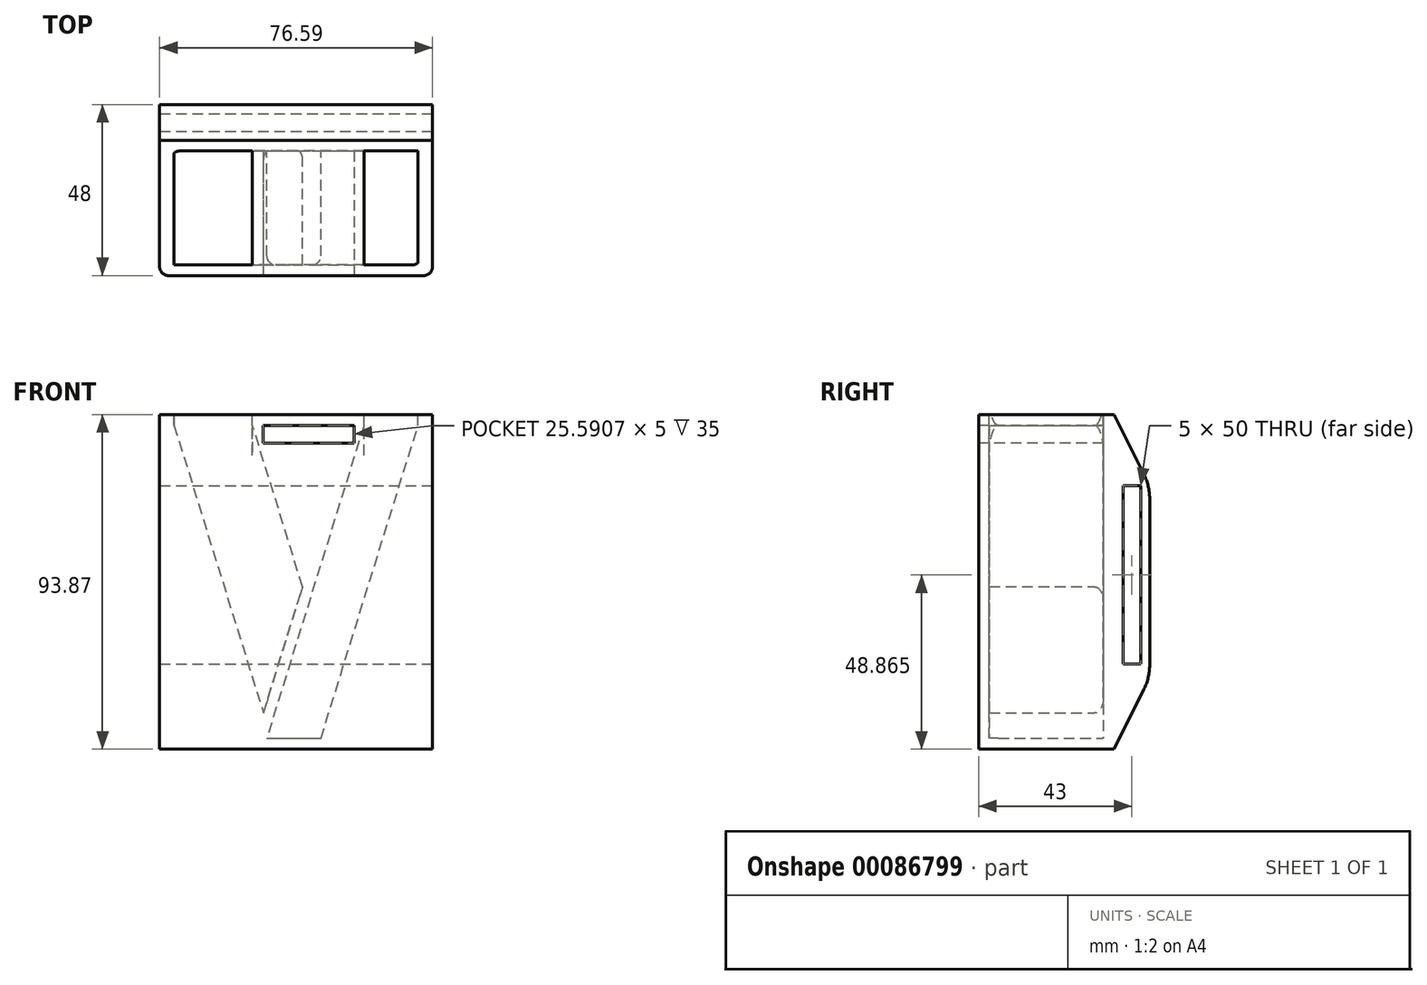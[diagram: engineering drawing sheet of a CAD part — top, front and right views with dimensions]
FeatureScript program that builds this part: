
annotation { "Feature Type Name" : "Feature", "Feature Type Description" : "" }
export const myFeature = defineFeature(function(context is Context, id is Id, definition is map)
    precondition{}
    {
        {
            var Q0;
            Q0=qCreatedBy(makeId("Front.planeOp"),FACE);
            var sketch = newSketch(context, id + "F0", { "sketchPlane" : qUnion([Q0])});
            skLineSegment(sketch, "E0", {"start": v(0, 0) * mm, "end": v(18.32, 0) * mm});
            skLineSegment(sketch, "E1", {"start": v(18.32, 0) * mm, "end": v(47.46, 93.87) * mm});
            skLineSegment(sketch, "E2", {"start": v(47.46, 93.87) * mm, "end": v(-29.13, 93.87) * mm});
            skLineSegment(sketch, "E3", {"start": v(-29.13, 93.87) * mm, "end": v(0, 0) * mm});
            skLineSegment(sketch, "E4", {"start": v(16.11, 3) * mm, "end": v(43.38, 90.87) * mm});
            skLineSegment(sketch, "E5", {"start": v(28.2, 90.87) * mm, "end": v(0.93, 3) * mm});
            skLineSegment(sketch, "E6", {"start": v(0, 10.12) * mm, "end": v(11, 45.54) * mm});
            skLineSegment(sketch, "E7", {"start": v(11, 45.54) * mm, "end": v(-3.07, 90.87) * mm});
            skLineSegment(sketch, "E8", {"start": v(-3.07, 90.87) * mm, "end": v(-25.06, 90.87) * mm, "construction": true});
            skLineSegment(sketch, "E9", {"start": v(-25.06, 90.87) * mm, "end": v(0, 10.12) * mm});
            skLineSegment(sketch, "E10", {"start": v(0.93, 3) * mm, "end": v(16.11, 3) * mm});
            skLineSegment(sketch, "E11", {"start": v(28.2, 90.87) * mm, "end": v(43.38, 90.87) * mm, "construction": true});
            skLineSegment(sketch, "E12", {"start": v(-14.07, 90.87) * mm, "end": v(5.5, 27.83) * mm, "construction": true});
            skLineSegment(sketch, "E13", {"start": v(-3.07, 90.87) * mm, "end": v(-3.07, 93.87) * mm});
            skLineSegment(sketch, "E14", {"start": v(-25.06, 90.87) * mm, "end": v(-25.06, 93.87) * mm});
            skLineSegment(sketch, "E15", {"start": v(28.2, 90.87) * mm, "end": v(28.2, 93.87) * mm});
            skLineSegment(sketch, "E16", {"start": v(43.38, 90.87) * mm, "end": v(43.38, 93.87) * mm});
            skLineSegment(sketch, "E17", {"start": v(-29.13, 93.87) * mm, "end": v(-29.13, 0) * mm});
            skLineSegment(sketch, "E18", {"start": v(-29.13, 0) * mm, "end": v(0, 0) * mm});
            skLineSegment(sketch, "E19", {"start": v(18.32, 0) * mm, "end": v(47.46, 0) * mm});
            skLineSegment(sketch, "E20", {"start": v(47.46, 0) * mm, "end": v(47.46, 93.87) * mm});
            skSolve(sketch);
        }
        {
            var Q0;
            Q0=makeQuery(id+"F0.imprint","IMPRINT",FACE,{"disambiguationData":[TD([[makeQuery(id+"F0.imprint","IMPRINT",EDGE,{"derivedFrom":sQuery(id+"F0.wireOp",EDGE,"E0")}),1.0]])]});
            var Q1;
            Q1=makeQuery(id+"F0.imprint","IMPRINT",FACE,{"disambiguationData":[TD([[makeQuery(id+"F0.imprint","IMPRINT",EDGE,{"derivedFrom":sQuery(id+"F0.wireOp",EDGE,"E6")}),1.0]])]});
            var Q2;
            Q2=makeQuery(id+"F0.imprint","IMPRINT",FACE,{"disambiguationData":[TD([[makeQuery(id+"F0.imprint","IMPRINT",EDGE,{"derivedFrom":sQuery(id+"F0.wireOp",EDGE,"E4")}),1.0]])]});
            var Q3;
            Q3=makeQuery(id+"F0.imprint","IMPRINT",FACE,{"disambiguationData":[TD([[makeQuery(id+"F0.imprint","IMPRINT",EDGE,{"derivedFrom":sQuery(id+"F0.wireOp",EDGE,"E3")}),-1.0]])]});
            var Q4;
            Q4=makeQuery(id+"F0.imprint","IMPRINT",FACE,{"disambiguationData":[TD([[makeQuery(id+"F0.imprint","IMPRINT",EDGE,{"derivedFrom":sQuery(id+"F0.wireOp",EDGE,"E1")}),-1.0]])]});
            extrude(context, id + "F1", {"entities" : qUnion([Q0, Q1, Q2, Q3, Q4]), "depth" : 3 * mm});
        }
        {
            var Q0;
            Q0=makeQuery(id+"F0.imprint","IMPRINT",FACE,{"disambiguationData":[TD([[makeQuery(id+"F0.imprint","IMPRINT",EDGE,{"derivedFrom":sQuery(id+"F0.wireOp",EDGE,"E0")}),1.0]])]});
            var Q1;
            Q1=makeQuery(id+"F0.imprint","IMPRINT",FACE,{"disambiguationData":[TD([[makeQuery(id+"F0.imprint","IMPRINT",EDGE,{"derivedFrom":sQuery(id+"F0.wireOp",EDGE,"E3")}),-1.0]])]});
            var Q2;
            Q2=makeQuery(id+"F0.imprint","IMPRINT",FACE,{"disambiguationData":[TD([[makeQuery(id+"F0.imprint","IMPRINT",EDGE,{"derivedFrom":sQuery(id+"F0.wireOp",EDGE,"E1")}),-1.0]])]});
            extrude(context, id + "F2", {"entities" : qUnion([Q0, Q1, Q2]), "operationType" : NewBodyOperationType.ADD, "depth" : 35 * mm, "hasSecondDirection" : true, "secondDirectionOppositeDirection" : false, "secondDirectionDepth" : 3 * mm});
        }
        {
            var Q0;
            Q0=makeQuery(id+"F0.imprint","IMPRINT",FACE,{"disambiguationData":[TD([[makeQuery(id+"F0.imprint","IMPRINT",EDGE,{"derivedFrom":sQuery(id+"F0.wireOp",EDGE,"E0")}),1.0]])]});
            var Q1;
            Q1=makeQuery(id+"F0.imprint","IMPRINT",FACE,{"disambiguationData":[TD([[makeQuery(id+"F0.imprint","IMPRINT",EDGE,{"derivedFrom":sQuery(id+"F0.wireOp",EDGE,"E6")}),1.0]])]});
            var Q2;
            Q2=makeQuery(id+"F0.imprint","IMPRINT",FACE,{"disambiguationData":[TD([[makeQuery(id+"F0.imprint","IMPRINT",EDGE,{"derivedFrom":sQuery(id+"F0.wireOp",EDGE,"E4")}),1.0]])]});
            var Q3;
            Q3=makeQuery(id+"F0.imprint","IMPRINT",FACE,{"disambiguationData":[TD([[makeQuery(id+"F0.imprint","IMPRINT",EDGE,{"derivedFrom":sQuery(id+"F0.wireOp",EDGE,"E3")}),-1.0]])]});
            var Q4;
            Q4=makeQuery(id+"F0.imprint","IMPRINT",FACE,{"disambiguationData":[TD([[makeQuery(id+"F0.imprint","IMPRINT",EDGE,{"derivedFrom":sQuery(id+"F0.wireOp",EDGE,"E1")}),-1.0]])]});
            extrude(context, id + "F3", {"entities" : qUnion([Q0, Q1, Q2, Q3, Q4]), "operationType" : NewBodyOperationType.ADD, "depth" : 38 * mm, "hasSecondDirection" : true, "secondDirectionOppositeDirection" : false, "secondDirectionDepth" : 35 * mm});
        }
        {
            var Q0;
            {var subQ0=sQuery(id+"F0.wireOp",EDGE,"E20");Q0=makeQuery(id+"F3.boolean.opBoolean","MERGE",FACE,{"derivedFrom":[makeQuery(id+"F2.boolean.opBoolean","MERGE",FACE,{"derivedFrom":[makeQuery(id+"F1.opExtrude","SWEPT_FACE",FACE,{"disambiguationData":[OSD([subQ0])]}),makeQuery(id+"F2.opExtrude","SWEPT_FACE",FACE,{"disambiguationData":[OSD([subQ0])]})]}),makeQuery(id+"F3.opExtrude","SWEPT_FACE",FACE,{"disambiguationData":[OSD([subQ0])]})]});}
            var sketch = newSketch(context, id + "F4", { "sketchPlane" : qUnion([Q0])});
            skLineSegment(sketch, "E21", {"start": v(0, 93.87) * mm, "end": v(10, 73.87) * mm});
            skLineSegment(sketch, "E22", {"start": v(10, 73.87) * mm, "end": v(10, 20) * mm});
            skLineSegment(sketch, "E23", {"start": v(10, 20) * mm, "end": v(0, 0) * mm});
            skLineSegment(sketch, "E24.bottom", {"start": v(2.5, 73.87) * mm, "end": v(7.5, 73.87) * mm});
            skLineSegment(sketch, "E24.top", {"start": v(2.5, 23.87) * mm, "end": v(7.5, 23.87) * mm});
            skLineSegment(sketch, "E24.left", {"start": v(2.5, 73.87) * mm, "end": v(2.5, 23.87) * mm});
            skLineSegment(sketch, "E24.right", {"start": v(7.5, 73.87) * mm, "end": v(7.5, 23.87) * mm});
            skSolve(sketch);
        }
        {
            var Q0;
            Q0=makeQuery(id+"F4.imprint","IMPRINT",FACE,{"disambiguationData":[TD([[makeQuery(id+"F4.imprint","IMPRINT",EDGE,{"derivedFrom":sQuery(id+"F4.wireOp",EDGE,"E21")}),-1.0]])]});
            var Q1;
            {var subQ0=sQuery(id+"F0.wireOp",EDGE,"E17");Q1=makeQuery(id+"F3.boolean.opBoolean","MERGE",FACE,{"derivedFrom":[makeQuery(id+"F2.boolean.opBoolean","MERGE",FACE,{"derivedFrom":[makeQuery(id+"F1.opExtrude","SWEPT_FACE",FACE,{"disambiguationData":[OSD([subQ0])]}),makeQuery(id+"F2.opExtrude","SWEPT_FACE",FACE,{"disambiguationData":[OSD([subQ0])]})]}),makeQuery(id+"F3.opExtrude","SWEPT_FACE",FACE,{"disambiguationData":[OSD([subQ0])]})]});}
            extrude(context, id + "F5", {"entities" : qUnion([Q0]), "operationType" : NewBodyOperationType.ADD, "endBound" : BoundingType.UP_TO_SURFACE, "oppositeDirection" : true, "endBoundEntityFace" : qUnion([Q1]), "depth" : 25 * mm});
        }
        {
            var Q0;
            Q0=makeQuery(id+"F5.opExtrude","SWEPT_EDGE",EDGE,{"disambiguationData":[OSD([sQuery(id+"F4.wireOp",EDGE,"E21"),sQuery(id+"F4.wireOp",EDGE,"E22")])]});
            var Q1;
            Q1=makeQuery(id+"F5.opExtrude","SWEPT_EDGE",EDGE,{"disambiguationData":[OSD([sQuery(id+"F4.wireOp",EDGE,"E22"),sQuery(id+"F4.wireOp",EDGE,"E23")])]});
            fillet(context, id + "F6", {"entities" : qUnion([Q0, Q1]), "radius" : 15 * mm, "tangentPropagation" : true, "allowEdgeOverflow" : false});
        }
        {
            var Q0;
            Q0=makeQuery(id+"F3.opExtrude","CAP_FACE",FACE,{"disambiguationData":[OSD([sQuery(id+"F0.wireOp",EDGE,"E0"),sQuery(id+"F0.wireOp",EDGE,"E2"),sQuery(id+"F0.wireOp",EDGE,"E17"),sQuery(id+"F0.wireOp",EDGE,"E18"),sQuery(id+"F0.wireOp",EDGE,"E19"),sQuery(id+"F0.wireOp",EDGE,"E20")])],"isStart":false});
            var sketch = newSketch(context, id + "F7", { "sketchPlane" : qUnion([Q0])});
            skLineSegment(sketch, "E25.right", {"start": v(25.46, 90.87) * mm, "end": v(25.46, 85.87) * mm});
            skLineSegment(sketch, "E26", {"start": v(25.46, 85.87) * mm, "end": v(-0.13, 85.87) * mm});
            skLineSegment(sketch, "E27", {"start": v(-0.13, 85.87) * mm, "end": v(-0.13, 90.87) * mm});
            skLineSegment(sketch, "E28", {"start": v(-0.13, 90.87) * mm, "end": v(25.46, 90.87) * mm});
            skSolve(sketch);
        }
        {
            var Q0;
            Q0=makeQuery(id+"F2.opExtrude","CAP_EDGE",EDGE,{"disambiguationData":[OSD([sQuery(id+"F0.wireOp",EDGE,"E9")])],"isStart":true});
            var Q1;
            Q1=makeQuery(id+"F2.opExtrude","CAP_EDGE",EDGE,{"disambiguationData":[OSD([sQuery(id+"F0.wireOp",EDGE,"E7")])],"isStart":true});
            var Q2;
            Q2=makeQuery(id+"F2.opExtrude","CAP_EDGE",EDGE,{"disambiguationData":[OSD([sQuery(id+"F0.wireOp",EDGE,"E7")])],"isStart":false});
            var Q3;
            Q3=makeQuery(id+"F2.opExtrude","CAP_EDGE",EDGE,{"disambiguationData":[OSD([sQuery(id+"F0.wireOp",EDGE,"E9")])],"isStart":false});
            var Q4;
            Q4=makeQuery(id+"F2.opExtrude","CAP_EDGE",EDGE,{"disambiguationData":[OSD([sQuery(id+"F0.wireOp",EDGE,"E4")])],"isStart":false});
            var Q5;
            Q5=makeQuery(id+"F2.opExtrude","CAP_EDGE",EDGE,{"disambiguationData":[OSD([sQuery(id+"F0.wireOp",EDGE,"E4")])],"isStart":true});
            var Q6;
            Q6=makeQuery(id+"F2.opExtrude","CAP_EDGE",EDGE,{"disambiguationData":[OSD([sQuery(id+"F0.wireOp",EDGE,"E5")])],"isStart":true});
            var Q7;
            Q7=makeQuery(id+"F2.opExtrude","CAP_EDGE",EDGE,{"disambiguationData":[OSD([sQuery(id+"F0.wireOp",EDGE,"E5")])],"isStart":false});
            fillet(context, id + "F8", {"entities" : qUnion([Q0, Q1, Q2, Q3, Q4, Q5, Q6, Q7]), "radius" : 2.5 * mm, "tangentPropagation" : true, "allowEdgeOverflow" : false});
        }
        {
            var Q0;
            Q0=makeQuery(id+"F3.opExtrude","CAP_EDGE",EDGE,{"disambiguationData":[OSD([sQuery(id+"F0.wireOp",EDGE,"E17")])],"isStart":false});
            var Q1;
            Q1=makeQuery(id+"F3.opExtrude","CAP_EDGE",EDGE,{"disambiguationData":[OSD([sQuery(id+"F0.wireOp",EDGE,"E20")])],"isStart":false});
            fillet(context, id + "F9", {"entities" : qUnion([Q0, Q1]), "radius" : 2.5 * mm, "tangentPropagation" : true, "allowEdgeOverflow" : false});
        }
        {
            var Q0;
            Q0 = qSketchRegion(id + "F7", true);
            extrude(context, id + "F10", {"entities" : qUnion([Q0]), "operationType" : NewBodyOperationType.REMOVE, "oppositeDirection" : true, "depth" : 35 * mm});
        }
    });
